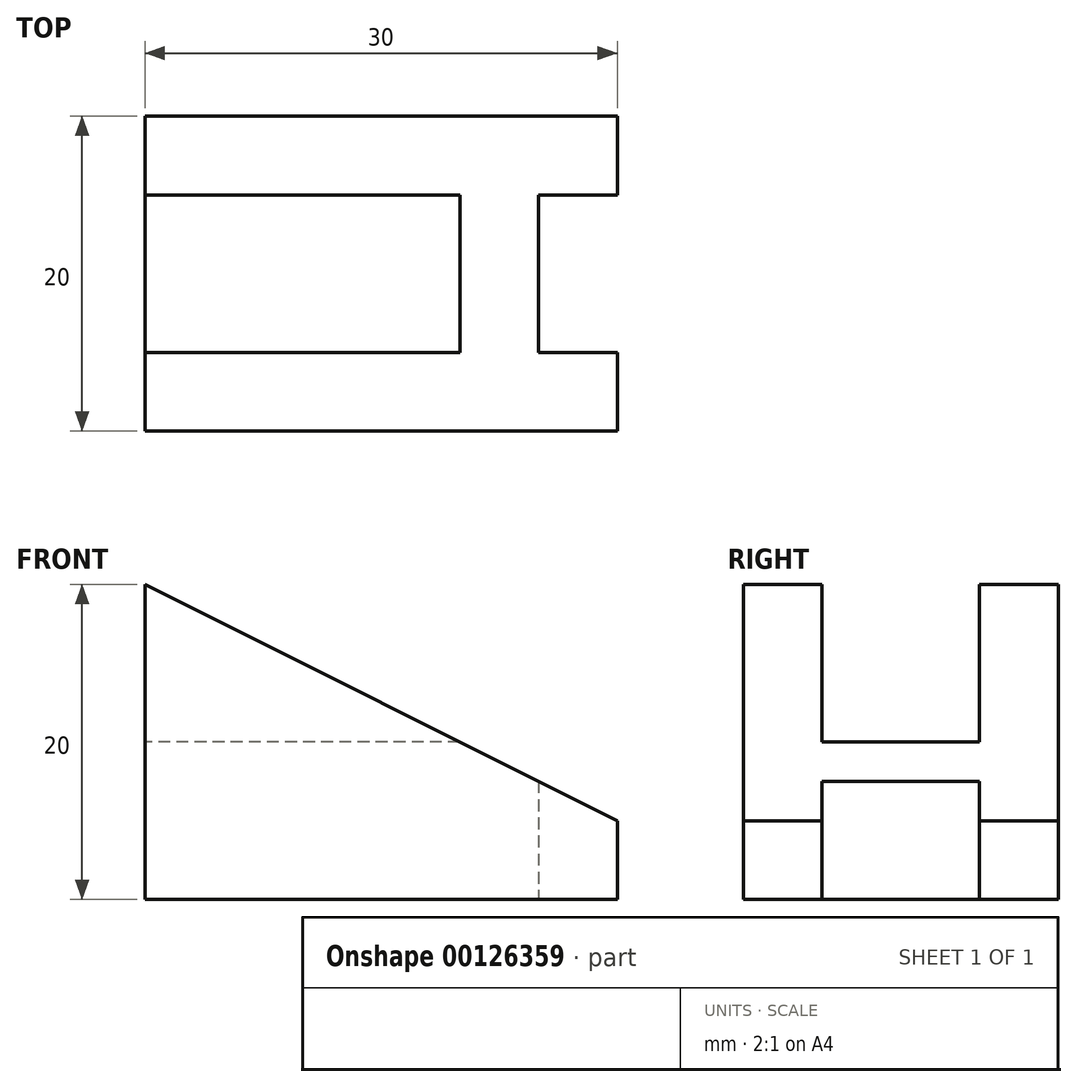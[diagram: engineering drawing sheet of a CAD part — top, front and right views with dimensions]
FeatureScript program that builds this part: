
annotation { "Feature Type Name" : "Feature", "Feature Type Description" : "" }
export const myFeature = defineFeature(function(context is Context, id is Id, definition is map)
    precondition{}
    {
        {
            var Q0;
            Q0=qCreatedBy(makeId("Front.planeOp"),FACE);
            var sketch = newSketch(context, id + "F0", { "sketchPlane" : qUnion([Q0])});
            skLineSegment(sketch, "E0", {"start": v(0, 0) * mm, "end": v(0, 20) * mm});
            skLineSegment(sketch, "E1", {"start": v(0, 20) * mm, "end": v(30, 5) * mm});
            skLineSegment(sketch, "E2", {"start": v(30, 5) * mm, "end": v(30, 0) * mm});
            skLineSegment(sketch, "E3", {"start": v(30, 0) * mm, "end": v(0, 0) * mm});
            skSolve(sketch);
        }
        {
            var Q0;
            Q0 = qSketchRegion(id + "F0", true);
            extrude(context, id + "F1", {"entities" : qUnion([Q0]), "endBound" : BoundingType.SYMMETRIC, "depth" : 20 * mm});
        }
        {
            var Q0;
            Q0=makeQuery(id+"F1.opExtrude","SWEPT_FACE",FACE,{"disambiguationData":[OSD([sQuery(id+"F0.wireOp",EDGE,"E0")])]});
            var sketch = newSketch(context, id + "F2", { "sketchPlane" : qUnion([Q0])});
            skLineSegment(sketch, "E4.bottom", {"start": v(-5, 20) * mm, "end": v(5, 20) * mm});
            skLineSegment(sketch, "E4.top", {"start": v(-5, 10) * mm, "end": v(5, 10) * mm});
            skLineSegment(sketch, "E4.left", {"start": v(-5, 20) * mm, "end": v(-5, 10) * mm});
            skLineSegment(sketch, "E4.right", {"start": v(5, 20) * mm, "end": v(5, 10) * mm});
            skSolve(sketch);
        }
        {
            var Q0;
            Q0 = qSketchRegion(id + "F2", true);
            extrude(context, id + "F3", {"entities" : qUnion([Q0]), "operationType" : NewBodyOperationType.REMOVE, "endBound" : BoundingType.THROUGH_ALL, "oppositeDirection" : true, "depth" : 25 * mm});
        }
        {
            var Q0;
            Q0=makeQuery(id+"F1.opExtrude","SWEPT_FACE",FACE,{"disambiguationData":[OSD([sQuery(id+"F0.wireOp",EDGE,"E3")])]});
            var sketch = newSketch(context, id + "F4", { "sketchPlane" : qUnion([Q0])});
            skLineSegment(sketch, "E5.bottom", {"start": v(30, 5) * mm, "end": v(25, 5) * mm});
            skLineSegment(sketch, "E5.top", {"start": v(30, -5) * mm, "end": v(25, -5) * mm});
            skLineSegment(sketch, "E5.left", {"start": v(30, 5) * mm, "end": v(30, -5) * mm});
            skLineSegment(sketch, "E5.right", {"start": v(25, 5) * mm, "end": v(25, -5) * mm});
            skSolve(sketch);
        }
        {
            var Q0;
            Q0 = qSketchRegion(id + "F4", true);
            extrude(context, id + "F5", {"entities" : qUnion([Q0]), "operationType" : NewBodyOperationType.REMOVE, "endBound" : BoundingType.THROUGH_ALL, "oppositeDirection" : true, "depth" : 25 * mm});
        }
    });
